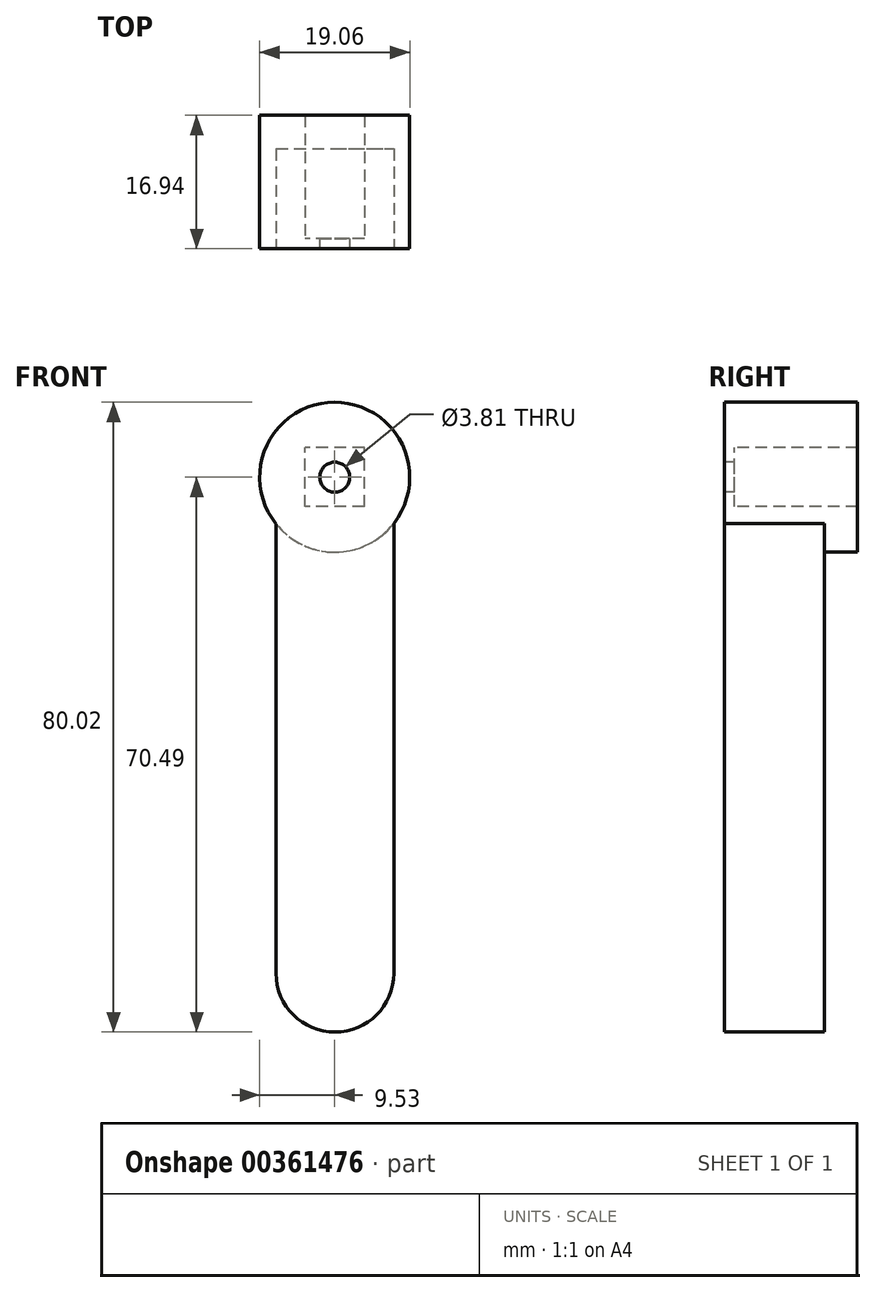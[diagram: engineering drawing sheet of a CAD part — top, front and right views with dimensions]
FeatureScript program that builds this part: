
annotation { "Feature Type Name" : "Feature", "Feature Type Description" : "" }
export const myFeature = defineFeature(function(context is Context, id is Id, definition is map)
    precondition{}
    {
        {
            var Q0;
            Q0=qCreatedBy(makeId("Front.planeOp"),FACE);
            var sketch = newSketch(context, id + "F0", { "sketchPlane" : qUnion([Q0])});
            skCircle(sketch, "E0", {"center": v(0, 0) * mm, "radius": 9.53 * mm});
            skLineSegment(sketch, "E1", {"start": v(-7.45, -5.93) * mm, "end": v(-7.45, -63.02) * mm});
            skLineSegment(sketch, "E2", {"start": v(7.5, -5.87) * mm, "end": v(7.5, -63.02) * mm});
            skArc(sketch, "E3", {"start": v(-7.45, -63.02) * mm, "mid": v(0.03, -70.5) * mm, "end": v(7.5, -63.02) * mm});
            skCircle(sketch, "E4", {"center": v(0, 0) * mm, "radius": 1.9 * mm});
            skLineSegment(sketch, "E5.bottom", {"start": v(3.75, -3.75) * mm, "end": v(-3.75, -3.75) * mm});
            skLineSegment(sketch, "E5.top", {"start": v(3.75, 3.75) * mm, "end": v(-3.75, 3.75) * mm});
            skLineSegment(sketch, "E5.left", {"start": v(3.75, -3.75) * mm, "end": v(3.75, 3.75) * mm});
            skLineSegment(sketch, "E5.right", {"start": v(-3.75, -3.75) * mm, "end": v(-3.75, 3.75) * mm});
            skSolve(sketch);
        }
        {
            var Q0;
            {var subQ0=sQuery(id+"F0.wireOp",EDGE,"E0");var subQ1=makeQuery(id+"F0.imprint","INTERSECT",VERTEX,{"derivedFrom":[subQ0,sQuery(id+"F0.wireOp",EDGE,"E1")]});Q0=makeQuery(id+"F0.imprint","IMPRINT",FACE,{"disambiguationData":[TD([[makeQuery(id+"F0.imprint","IMPRINT",EDGE,{"disambiguationData":[TD([[subQ1,-1.0]])],"derivedFrom":subQ0}),1.0]])]});}
            extrude(context, id + "F1", {"entities" : qUnion([Q0]), "oppositeDirection" : true, "depth" : 16.94 * mm});
        }
        {
            var Q0;
            {var subQ0=sQuery(id+"F0.wireOp",EDGE,"E1");Q0=makeQuery(id+"F0.imprint","IMPRINT",FACE,{"disambiguationData":[TD([[makeQuery(id+"F0.imprint","IMPRINT",EDGE,{"derivedFrom":subQ0}),1.0]])]});}
            extrude(context, id + "F2", {"entities" : qUnion([Q0]), "operationType" : NewBodyOperationType.ADD, "oppositeDirection" : true, "depth" : 12.7 * mm});
        }
        {
            var Q0;
            Q0=makeQuery(id+"F0.imprint","IMPRINT",FACE,{"disambiguationData":[TD([[makeQuery(id+"F0.imprint","IMPRINT",EDGE,{"derivedFrom":sQuery(id+"F0.wireOp",EDGE,"E4")}),-1.0]])]});
            extrude(context, id + "F3", {"entities" : qUnion([Q0]), "operationType" : NewBodyOperationType.ADD, "oppositeDirection" : true, "depth" : 1.27 * mm});
        }
    });
